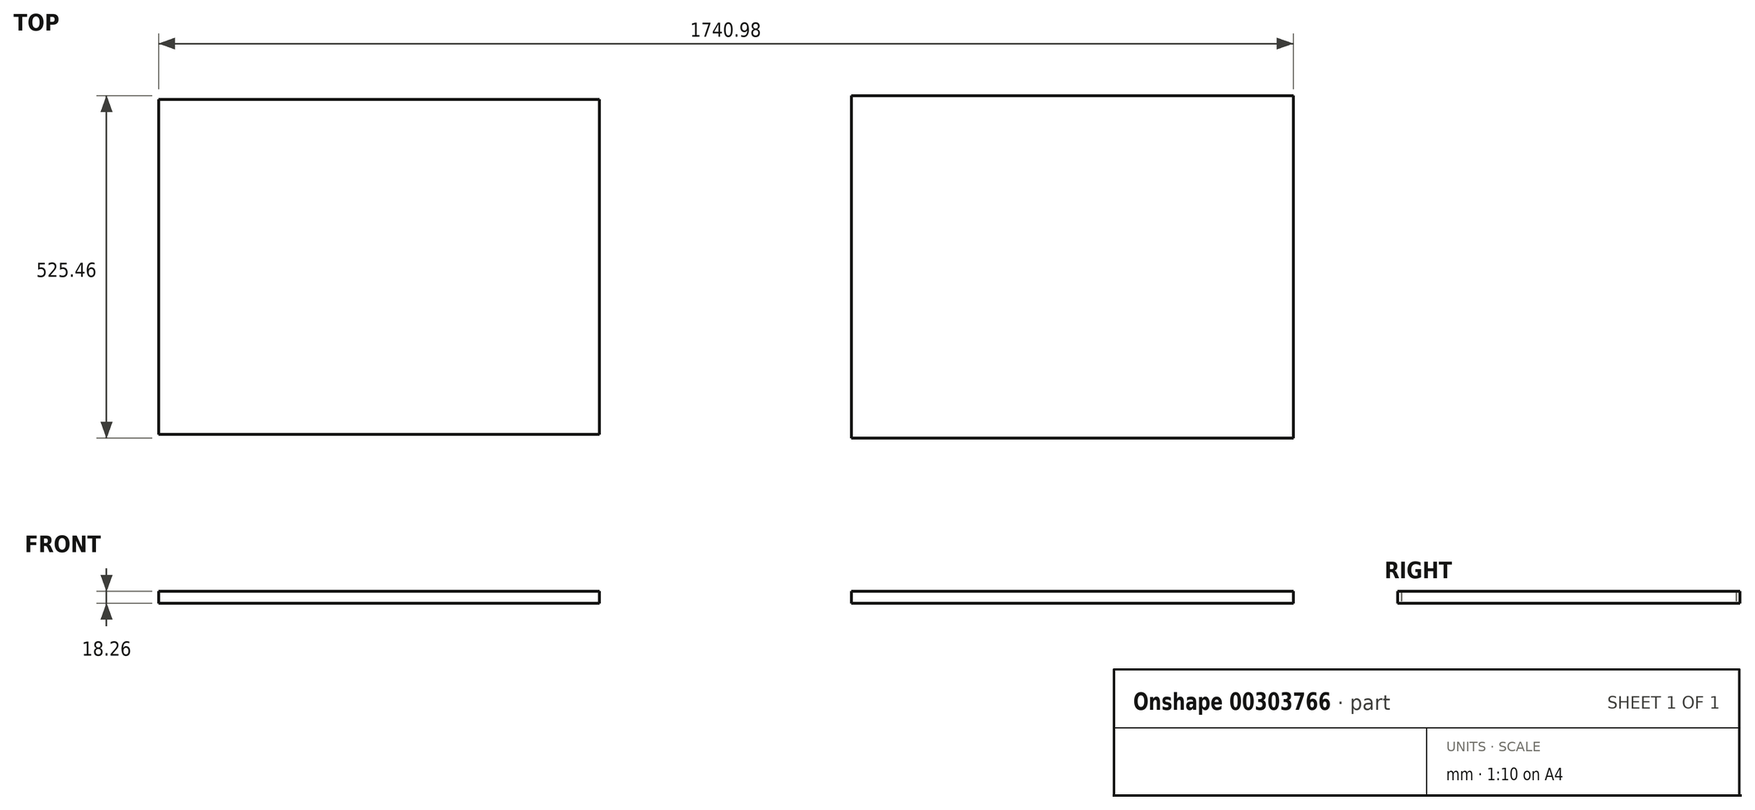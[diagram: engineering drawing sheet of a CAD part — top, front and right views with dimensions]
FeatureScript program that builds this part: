
annotation { "Feature Type Name" : "Feature", "Feature Type Description" : "" }
export const myFeature = defineFeature(function(context is Context, id is Id, definition is map)
    precondition{}
    {
        {
            var Q0;
            Q0=qCreatedBy(makeId("Top.planeOp"),FACE);
            var sketch = newSketch(context, id + "F0", { "sketchPlane" : qUnion([Q0])});
            skLineSegment(sketch, "E0.bottom", {"start": v(-882.8, 256.78) * mm, "end": v(-206.52, 256.78) * mm});
            skLineSegment(sketch, "E0.top", {"start": v(-882.8, -256.78) * mm, "end": v(-206.52, -256.78) * mm});
            skLineSegment(sketch, "E0.left", {"start": v(-882.8, 256.78) * mm, "end": v(-882.8, -256.78) * mm});
            skLineSegment(sketch, "E0.right", {"start": v(-206.52, 256.78) * mm, "end": v(-206.52, -256.78) * mm});
            skPoint(sketch, "E0.middle", {"position": v(-544.66, 0) * mm});
            skLineSegment(sketch, "E1.bottom", {"start": v(858.19, 262.73) * mm, "end": v(180.33, 262.73) * mm});
            skLineSegment(sketch, "E1.top", {"start": v(858.19, -262.73) * mm, "end": v(180.33, -262.73) * mm});
            skLineSegment(sketch, "E1.left", {"start": v(858.19, 262.73) * mm, "end": v(858.19, -262.73) * mm});
            skLineSegment(sketch, "E1.right", {"start": v(180.33, 262.73) * mm, "end": v(180.33, -262.73) * mm});
            skPoint(sketch, "E1.middle", {"position": v(519.26, 0) * mm});
            skText(sketch, "E2", { "text": "LEFT\n", "fontName": "OpenSans-Regular.ttf"});
            skText(sketch, "E3", { "text": "RIGHT", "fontName": "OpenSans-Regular.ttf"});
            const initialGuessF0  = {"E2": [-0.74575, 0.29629, 1, 0, 0.06824], "E3": [0.38194, 0.28125, 1, 0, 0.08212]};
            skSetInitialGuess(sketch, initialGuessF0);
            skSolve(sketch);
        }
        {
            var Q0;
            Q0=makeQuery(id+"F0.imprint","IMPRINT",FACE,{"disambiguationData":[TD([[makeQuery(id+"F0.imprint","IMPRINT",EDGE,{"derivedFrom":sQuery(id+"F0.wireOp",EDGE,"E0.bottom")}),-1.0]])]});
            var Q1;
            Q1=makeQuery(id+"F0.imprint","IMPRINT",FACE,{"disambiguationData":[TD([[makeQuery(id+"F0.imprint","IMPRINT",EDGE,{"derivedFrom":sQuery(id+"F0.wireOp",EDGE,"E1.bottom")}),1.0]])]});
            extrude(context, id + "F1", {"entities" : qUnion([Q0, Q1]), "depth" : 18.26 * mm, "offsetDistance" : 25.4 * mm});
        }
    });
